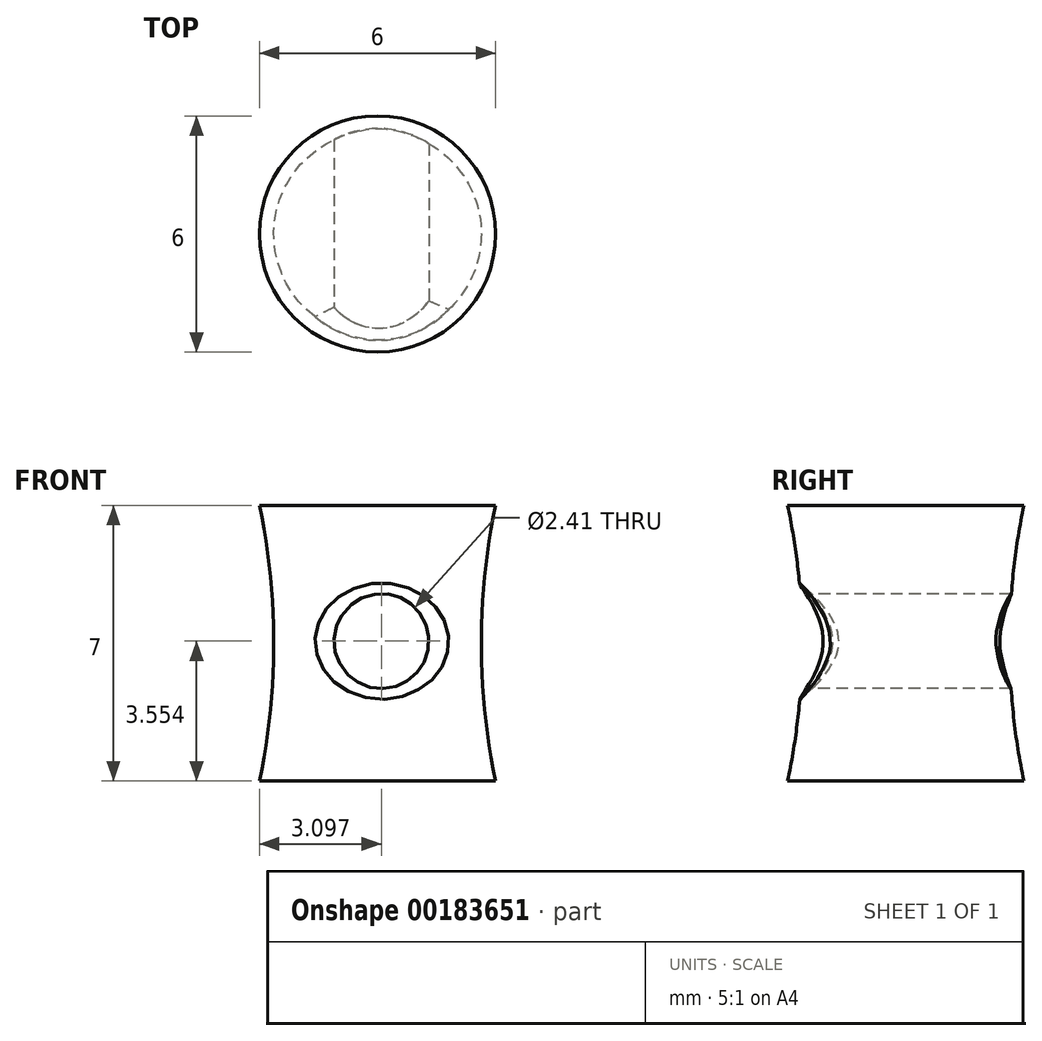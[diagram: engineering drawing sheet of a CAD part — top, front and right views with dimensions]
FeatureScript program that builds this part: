
annotation { "Feature Type Name" : "Feature", "Feature Type Description" : "" }
export const myFeature = defineFeature(function(context is Context, id is Id, definition is map)
    precondition{}
    {
        {
            var Q0;
            Q0=qCreatedBy(makeId("Front.planeOp"),FACE);
            var sketch = newSketch(context, id + "F0", { "sketchPlane" : qUnion([Q0])});
            skLineSegment(sketch, "E0.bottom", {"start": v(5.32, 34.64) * mm, "end": v(8.32, 34.64) * mm});
            skLineSegment(sketch, "E0.top", {"start": v(5.32, 27.64) * mm, "end": v(8.32, 27.64) * mm});
            skLineSegment(sketch, "E0.right", {"start": v(8.32, 34.64) * mm, "end": v(8.32, 27.64) * mm});
            skArc(sketch, "E1", {"start": v(5.32, 27.64) * mm, "mid": v(5.68, 31.14) * mm, "end": v(5.32, 34.64) * mm});
            skSolve(sketch);
        }
        {
            var Q0;
            Q0=makeQuery(id+"F0.imprint","IMPRINT",FACE,{"disambiguationData":[TD([[makeQuery(id+"F0.imprint","IMPRINT",EDGE,{"derivedFrom":sQuery(id+"F0.wireOp",EDGE,"E0.bottom")}),-1.0]])]});
            var Q1;
            Q1=sQuery(id+"F0.wireOp",EDGE,"E0.right");
            revolve(context, id + "F1", {"entities" : qUnion([Q0]), "axis" : qUnion([Q1]), "revolveType" : RevolveType.FULL});
        }
        {
            var Q0;
            Q0=qCreatedBy(makeId("Front.planeOp"),FACE);
            var sketch = newSketch(context, id + "F2", { "sketchPlane" : qUnion([Q0])});
            skCircle(sketch, "E2", {"center": v(8.42, 31.2) * mm, "radius": 1.2 * mm});
            skSolve(sketch);
        }
        {
            var Q0;
            Q0 = qSketchRegion(id + "F2", true);
            extrude(context, id + "F3", {"entities" : qUnion([Q0]), "operationType" : NewBodyOperationType.REMOVE, "endBound" : BoundingType.THROUGH_ALL, "oppositeDirection" : true, "depth" : 25 * mm, "hasSecondDirection" : true, "secondDirectionOppositeDirection" : false, "secondDirectionDepth" : 25 * mm});
        }
        {
            var Q0;
            Q0=makeQuery(id+"F3.boolean.opBoolean","INTERSECT",EDGE,{"disambiguationData":[OD(0.0)],"derivedFrom":[makeQuery(id+"F1.opRevolve","SWEPT_FACE",FACE,{"disambiguationData":[OSD([sQuery(id+"F0.wireOp",EDGE,"E1")])]}),makeQuery(id+"F3.opExtrude","SWEPT_FACE",FACE,{"disambiguationData":[OSD([sQuery(id+"F2.wireOp",EDGE,"E2")])]})]});
            chamfer(context, id + "F4", {"entities" : qUnion([Q0]), "width" : 0.3 * mm, "tangentPropagation" : true});
        }
    });
